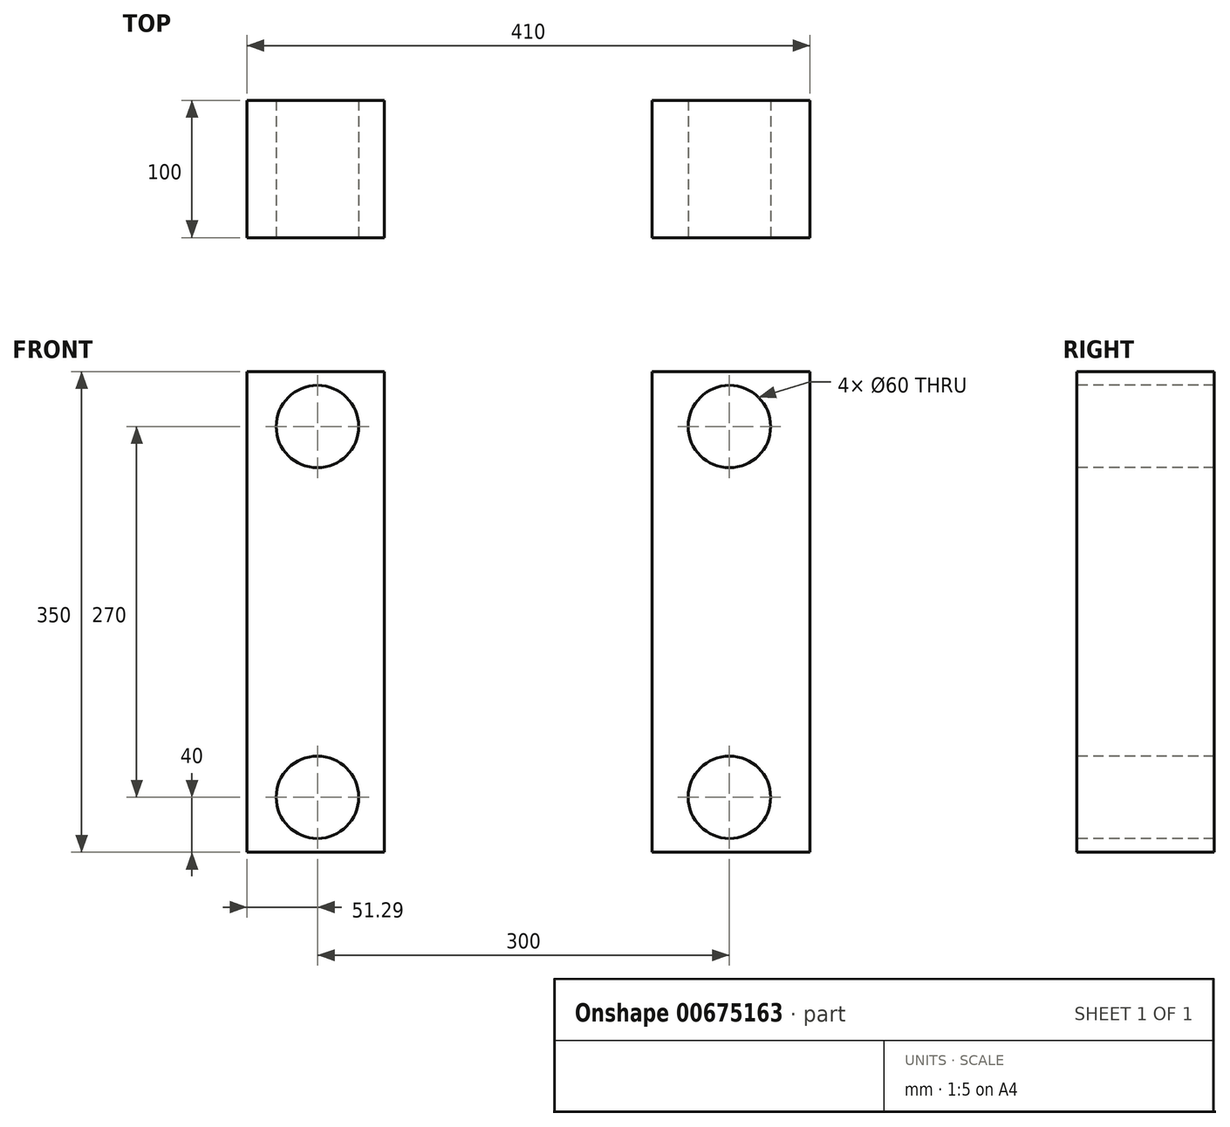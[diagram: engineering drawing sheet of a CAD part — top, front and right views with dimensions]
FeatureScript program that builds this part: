
annotation { "Feature Type Name" : "Feature", "Feature Type Description" : "" }
export const myFeature = defineFeature(function(context is Context, id is Id, definition is map)
    precondition{}
    {
        {
            var Q0;
            Q0=qCreatedBy(makeId("Top.planeOp"),FACE);
            var sketch = newSketch(context, id + "F0", { "sketchPlane" : qUnion([Q0])});
            skLineSegment(sketch, "E0.bottom", {"start": v(-201.29, 0) * mm, "end": v(-101.29, 0) * mm});
            skLineSegment(sketch, "E0.top", {"start": v(-201.29, -100) * mm, "end": v(-101.29, -100) * mm});
            skLineSegment(sketch, "E0.left", {"start": v(-201.29, 0) * mm, "end": v(-201.29, -100) * mm});
            skLineSegment(sketch, "E0.right", {"start": v(-101.29, 0) * mm, "end": v(-101.29, -100) * mm});
            skLineSegment(sketch, "E1.bottom", {"start": v(93.71, 0) * mm, "end": v(208.71, 0) * mm});
            skLineSegment(sketch, "E1.top", {"start": v(93.71, -100) * mm, "end": v(208.71, -100) * mm});
            skLineSegment(sketch, "E1.left", {"start": v(93.71, 0) * mm, "end": v(93.71, -100) * mm});
            skLineSegment(sketch, "E1.right", {"start": v(208.71, 0) * mm, "end": v(208.71, -100) * mm});
            skSolve(sketch);
        }
        {
            var Q0;
            Q0 = qSketchRegion(id + "F0", true);
            extrude(context, id + "F1", {"entities" : qUnion([Q0]), "depth" : 350 * mm, "offsetDistance" : 25 * mm});
        }
        {
            var Q0;
            Q0=makeQuery(id+"F1.opExtrude","SWEPT_FACE",FACE,{"disambiguationData":[OSD([sQuery(id+"F0.wireOp",EDGE,"E0.top")])]});
            var sketch = newSketch(context, id + "F2", { "sketchPlane" : qUnion([Q0])});
            skCircle(sketch, "E2", {"center": v(-150, 310) * mm, "radius": 30 * mm});
            skSolve(sketch);
        }
        {
            var Q0;
            Q0=makeQuery(id+"F2.imprint","IMPRINT",FACE,{"disambiguationData":[TD([[makeQuery(id+"F2.imprint","IMPRINT",EDGE,{"derivedFrom":sQuery(id+"F2.wireOp",EDGE,"E2")}),1.0]])]});
            extrude(context, id + "F3", {"entities" : qUnion([Q0]), "operationType" : NewBodyOperationType.REMOVE, "oppositeDirection" : true, "depth" : 200 * mm, "offsetDistance" : 25 * mm});
        }
        {
            var Q0;
            Q0=makeQuery(id+"F1.opExtrude","SWEPT_FACE",FACE,{"disambiguationData":[OSD([sQuery(id+"F0.wireOp",EDGE,"E1.top")])]});
            var sketch = newSketch(context, id + "F4", { "sketchPlane" : qUnion([Q0])});
            skCircle(sketch, "E3", {"center": v(150, 310) * mm, "radius": 30 * mm});
            skSolve(sketch);
        }
        {
            var Q0;
            Q0=makeQuery(id+"F4.imprint","IMPRINT",FACE,{"disambiguationData":[TD([[makeQuery(id+"F4.imprint","IMPRINT",EDGE,{"derivedFrom":sQuery(id+"F4.wireOp",EDGE,"E3")}),1.0]])]});
            extrude(context, id + "F5", {"entities" : qUnion([Q0]), "operationType" : NewBodyOperationType.REMOVE, "oppositeDirection" : true, "depth" : 200 * mm, "offsetDistance" : 25 * mm});
        }
        {
            var Q0;
            Q0=makeQuery(id+"F1.opExtrude","SWEPT_FACE",FACE,{"disambiguationData":[OSD([sQuery(id+"F0.wireOp",EDGE,"E0.top")])]});
            var sketch = newSketch(context, id + "F6", { "sketchPlane" : qUnion([Q0])});
            skCircle(sketch, "E4", {"center": v(-150, 40) * mm, "radius": 30 * mm});
            skSolve(sketch);
        }
        {
            var Q0;
            Q0=makeQuery(id+"F6.imprint","IMPRINT",FACE,{"disambiguationData":[TD([[makeQuery(id+"F6.imprint","IMPRINT",EDGE,{"derivedFrom":sQuery(id+"F6.wireOp",EDGE,"E4")}),1.0]])]});
            extrude(context, id + "F7", {"entities" : qUnion([Q0]), "operationType" : NewBodyOperationType.REMOVE, "oppositeDirection" : true, "depth" : 200 * mm, "offsetDistance" : 25 * mm});
        }
        {
            var Q0;
            Q0=makeQuery(id+"F1.opExtrude","SWEPT_FACE",FACE,{"disambiguationData":[OSD([sQuery(id+"F0.wireOp",EDGE,"E1.top")])]});
            var sketch = newSketch(context, id + "F8", { "sketchPlane" : qUnion([Q0])});
            skCircle(sketch, "E5", {"center": v(150, 40) * mm, "radius": 30 * mm});
            skSolve(sketch);
        }
        {
            var Q0;
            Q0=makeQuery(id+"F8.imprint","IMPRINT",FACE,{"disambiguationData":[TD([[makeQuery(id+"F8.imprint","IMPRINT",EDGE,{"derivedFrom":sQuery(id+"F8.wireOp",EDGE,"E5")}),1.0]])]});
            extrude(context, id + "F9", {"entities" : qUnion([Q0]), "operationType" : NewBodyOperationType.REMOVE, "oppositeDirection" : true, "depth" : 200 * mm, "offsetDistance" : 25 * mm});
        }
    });
